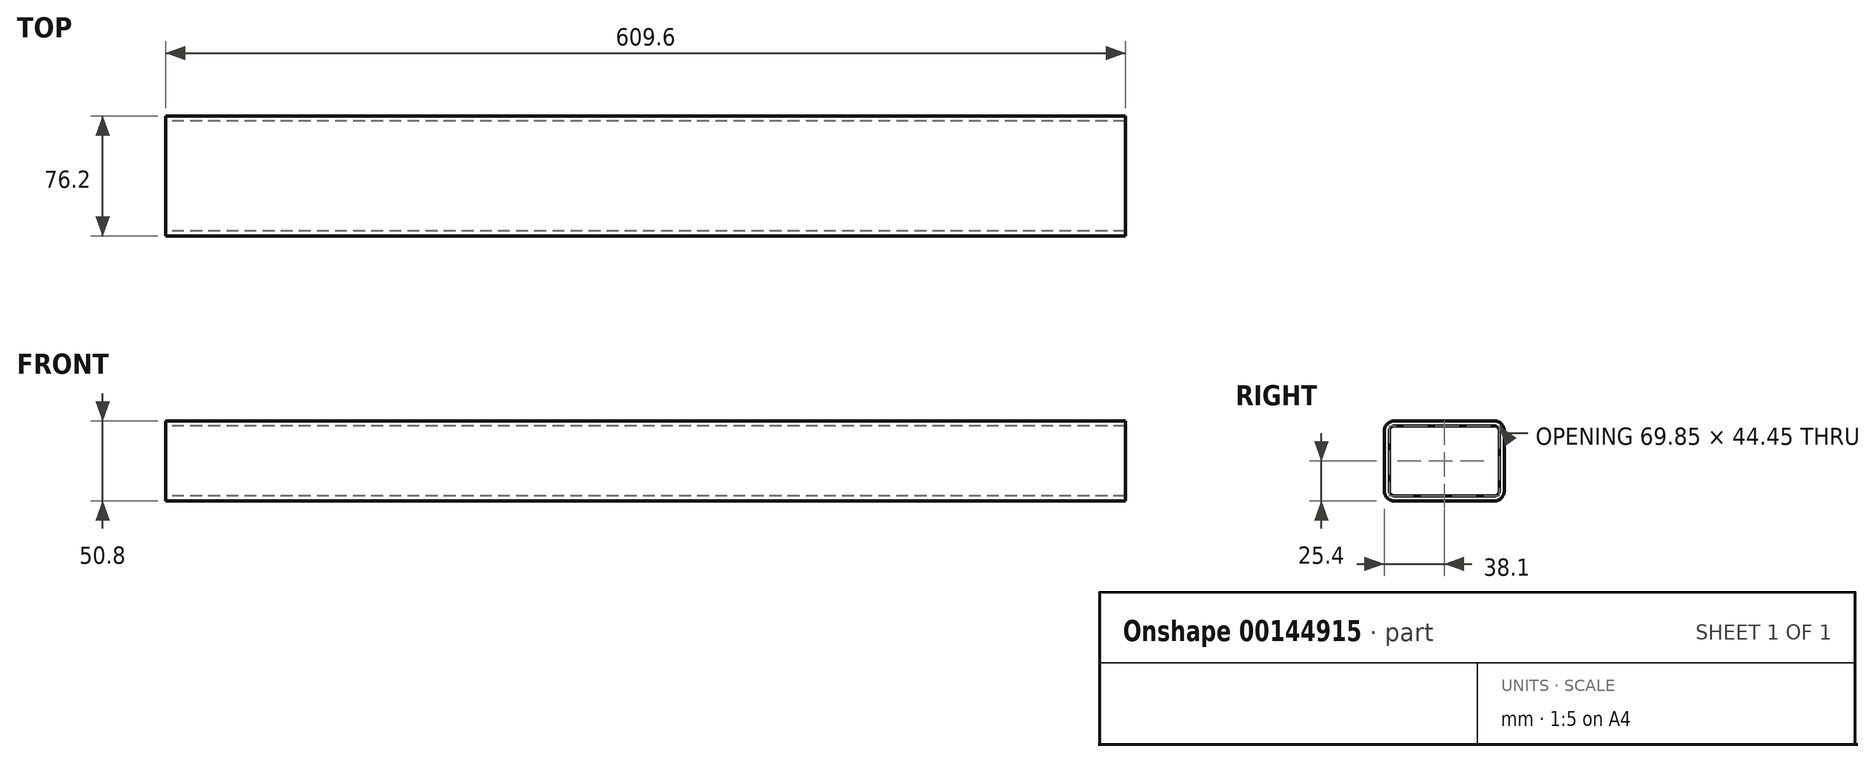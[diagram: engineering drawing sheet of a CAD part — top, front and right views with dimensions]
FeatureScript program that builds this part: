
annotation { "Feature Type Name" : "Feature", "Feature Type Description" : "" }
export const myFeature = defineFeature(function(context is Context, id is Id, definition is map)
    precondition{}
    {
        {
            var Q0;
            Q0=qCreatedBy(makeId("Right.planeOp"),FACE);
            var sketch = newSketch(context, id + "F0", { "sketchPlane" : qUnion([Q0])});
            skLineSegment(sketch, "E0.bottom", {"start": v(6.35, 0) * mm, "end": v(69.85, 0) * mm});
            skLineSegment(sketch, "E0.top", {"start": v(6.35, -50.8) * mm, "end": v(69.85, -50.8) * mm});
            skLineSegment(sketch, "E0.left", {"start": v(0, -6.35) * mm, "end": v(0, -44.45) * mm});
            skLineSegment(sketch, "E0.right", {"start": v(76.2, -6.35) * mm, "end": v(76.2, -44.45) * mm});
            skPoint(sketch, "E1.visualSharp", {"position": v(0, 0) * mm});
            skArc(sketch, "E1.filletArc", {"start": v(6.35, 0) * mm, "mid": v(1.86, -1.86) * mm, "end": v(0, -6.35) * mm});
            skPoint(sketch, "E2.visualSharp", {"position": v(76.2, 0) * mm});
            skArc(sketch, "E2.filletArc", {"start": v(76.2, -6.35) * mm, "mid": v(74.34, -1.86) * mm, "end": v(69.85, 0) * mm});
            skPoint(sketch, "E3.visualSharp", {"position": v(76.2, -50.8) * mm});
            skArc(sketch, "E3.filletArc", {"start": v(69.85, -50.8) * mm, "mid": v(74.34, -48.94) * mm, "end": v(76.2, -44.45) * mm});
            skPoint(sketch, "E4.visualSharp", {"position": v(0, -50.8) * mm});
            skArc(sketch, "E4.filletArc", {"start": v(0, -44.45) * mm, "mid": v(1.86, -48.94) * mm, "end": v(6.35, -50.8) * mm});
            skArc(sketch, "E5.0", {"start": v(6.35, -3.18) * mm, "mid": v(4.1, -4.1) * mm, "end": v(3.18, -6.35) * mm});
            skLineSegment(sketch, "E5.1", {"start": v(6.35, -3.18) * mm, "end": v(69.85, -3.18) * mm});
            skLineSegment(sketch, "E5.2", {"start": v(3.18, -6.35) * mm, "end": v(3.18, -44.45) * mm});
            skArc(sketch, "E5.3", {"start": v(73.03, -6.35) * mm, "mid": v(72.1, -4.1) * mm, "end": v(69.85, -3.17) * mm});
            skArc(sketch, "E5.4", {"start": v(3.18, -44.45) * mm, "mid": v(4.1, -46.7) * mm, "end": v(6.35, -47.62) * mm});
            skLineSegment(sketch, "E5.5", {"start": v(6.35, -47.63) * mm, "end": v(69.85, -47.63) * mm});
            skArc(sketch, "E5.6", {"start": v(69.85, -47.63) * mm, "mid": v(72.1, -46.7) * mm, "end": v(73.03, -44.45) * mm});
            skLineSegment(sketch, "E5.7", {"start": v(73.03, -6.35) * mm, "end": v(73.03, -44.45) * mm});
            skSolve(sketch);
        }
        {
            var Q0;
            Q0=makeQuery(id+"F0.imprint","IMPRINT",FACE,{"disambiguationData":[TD([[makeQuery(id+"F0.imprint","IMPRINT",EDGE,{"derivedFrom":sQuery(id+"F0.wireOp",EDGE,"E0.bottom")}),-1.0]])]});
            extrude(context, id + "F1", {"entities" : qUnion([Q0]), "depth" : 609.6 * mm});
        }
        {
            var Q0;
            Q0=makeQuery(id+"F1.opExtrude","SWEPT_FACE",FACE,{"disambiguationData":[OSD([sQuery(id+"F0.wireOp",EDGE,"E0.bottom")])]});
            var sketch = newSketch(context, id + "F2", { "sketchPlane" : qUnion([Q0])});
            skLineSegment(sketch, "E6.0", {"start": v(0, 6.35) * mm, "end": v(0, 69.85) * mm});
            skLineSegment(sketch, "E7.0", {"start": v(609.6, 76.2) * mm, "end": v(0, 76.2) * mm});
            skLineSegment(sketch, "E8", {"start": v(304.8, 76.2) * mm, "end": v(304.8, 0) * mm, "construction": true});
            skLineSegment(sketch, "E9", {"start": v(0, 38.1) * mm, "end": v(609.6, 38.1) * mm, "construction": true});
            skLineSegment(sketch, "E10.0", {"start": v(609.6, 6.35) * mm, "end": v(609.6, 69.85) * mm, "construction": true});
            skLineSegment(sketch, "E11.0", {"start": v(609.6, 0) * mm, "end": v(0, 0) * mm, "construction": true});
            skPoint(sketch, "E12", {"position": v(304.8, 38.1) * mm});
            skSolve(sketch);
        }
    });
